# Revit family: Thermostatic_Trim-GROHE-Allure_Brilliant-19794000-Updated
name_source: partatom
category: Plumbing Fixtures
units: mm (PartAtom-declared; Revit-internal decimal feet)

## family parameters
Cut with Voids When Loaded = No
Host = Face
OmniClass Number = 23.45.05.14.17
OmniClass Title = Showers
Part Type = Normal
Room Calculation Point = No
Round Connector Dimension = Use Diameter
Shared = Yes

## types (1)
- 19794000
    Assembly Code = D2010710
    CEC Compliant = Yes
    CW Connection = No
    CWFU = 0
    Default Elevation = 44"
    Description = Allure Brilliant Dual Function Thermostatic Trim with Control Module
    Finish = Metal-Grohe-StarLight_Chrome
    Flow Rate = 6.3 gpm at 45 psi (bottom outlet), 3.2 gpm at 45 psi (top outlet)
    HW Connection = No
    HWFU = 0
    Height = 6 11/16"
    IAPMO Compliance = ASME A112.18.1/CSA B125.1
    Installation Type = Wall Mounted
    Manufacturer = Grohe
    Material = Metal-Grohe-StarLight_Chrome
    Model = 19794000
    Price = Prices may vary. Please consult Manufacturer Representative for most up-to-date price list.
    Product Documentation Link = https://americanstandard.box.com
    Product Page URL = https://www.grohe.us
    Revised Date = 07/2/2021
    Shipping Weight = 6.230 lb
    Type Comments = 2-Way diverter function
    URL = https://www.grohe.us
    Vent Connection = No
    WFU = 0
    Warranty Documentation Link = https://cdn.cloud.grohe.com
    Warranty Information = Lifetime Limited Warranty
    Waste Connection = No
    Width = 6 11/16"

## geometry (parser evidence)
native form markers: Sweep x5
no freeform markers — native parametric forms only
